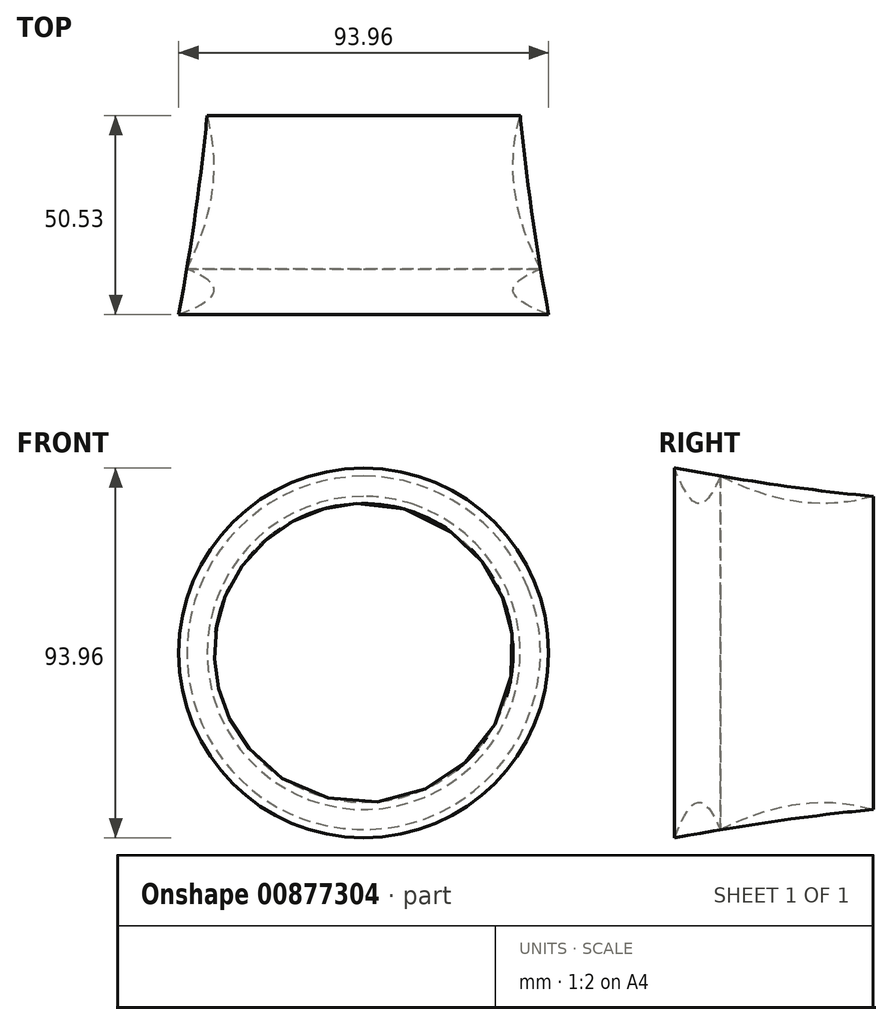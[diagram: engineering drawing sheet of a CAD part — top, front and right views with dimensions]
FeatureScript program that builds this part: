
annotation { "Feature Type Name" : "Feature", "Feature Type Description" : "" }
export const myFeature = defineFeature(function(context is Context, id is Id, definition is map)
    precondition{}
    {
        {
            var Q0;
            Q0=qCreatedBy(makeId("Front.planeOp"),FACE);
            var sketch = newSketch(context, id + "F0", { "sketchPlane" : qUnion([Q0])});
            skCircle(sketch, "E0.cCircle", {"center": v(-51.74, 37.96) * mm, "radius": 10.31 * mm, "construction": true});
            skLineSegment(sketch, "E0.0", {"start": v(-33.88, 27.65) * mm, "end": v(-69.6, 27.65) * mm});
            skLineSegment(sketch, "E0.1", {"start": v(-69.6, 27.65) * mm, "end": v(-51.74, 58.59) * mm});
            skLineSegment(sketch, "E0.2", {"start": v(-51.74, 58.59) * mm, "end": v(-33.88, 27.65) * mm});
            skPoint(sketch, "E0.0.midPoint", {"position": v(-51.74, 27.65) * mm});
            skSolve(sketch);
        }
        {
            var Q0;
            Q0=qCreatedBy(makeId("Top.planeOp"),FACE);
            var sketch = newSketch(context, id + "F1", { "sketchPlane" : qUnion([Q0])});
            skCircle(sketch, "E1.cCircle", {"center": v(-46.54, 44.96) * mm, "radius": 15.28 * mm, "construction": true});
            skLineSegment(sketch, "E1.0", {"start": v(-39.84, 74.78) * mm, "end": v(-24.06, 24.25) * mm});
            skLineSegment(sketch, "E1.1", {"start": v(-24.06, 24.25) * mm, "end": v(-75.72, 35.85) * mm});
            skLineSegment(sketch, "E1.2", {"start": v(-75.72, 35.85) * mm, "end": v(-39.84, 74.78) * mm});
            skPoint(sketch, "E1.0.midPoint", {"position": v(-31.95, 49.52) * mm});
            skSolve(sketch);
        }
        {
            var Q0;
            Q0 = qSketchRegion(id + "F1", true);
            var Q1;
            Q1=sQuery(id+"F0.wireOp",EDGE,"E0.cCircle");
            revolve(context, id + "F2", {"surfaceOperationType" : NewSurfaceOperationType.NEW, "entities" : qUnion([Q0]), "axis" : qUnion([Q1]), "revolveType" : RevolveType.FULL});
        }
    });
